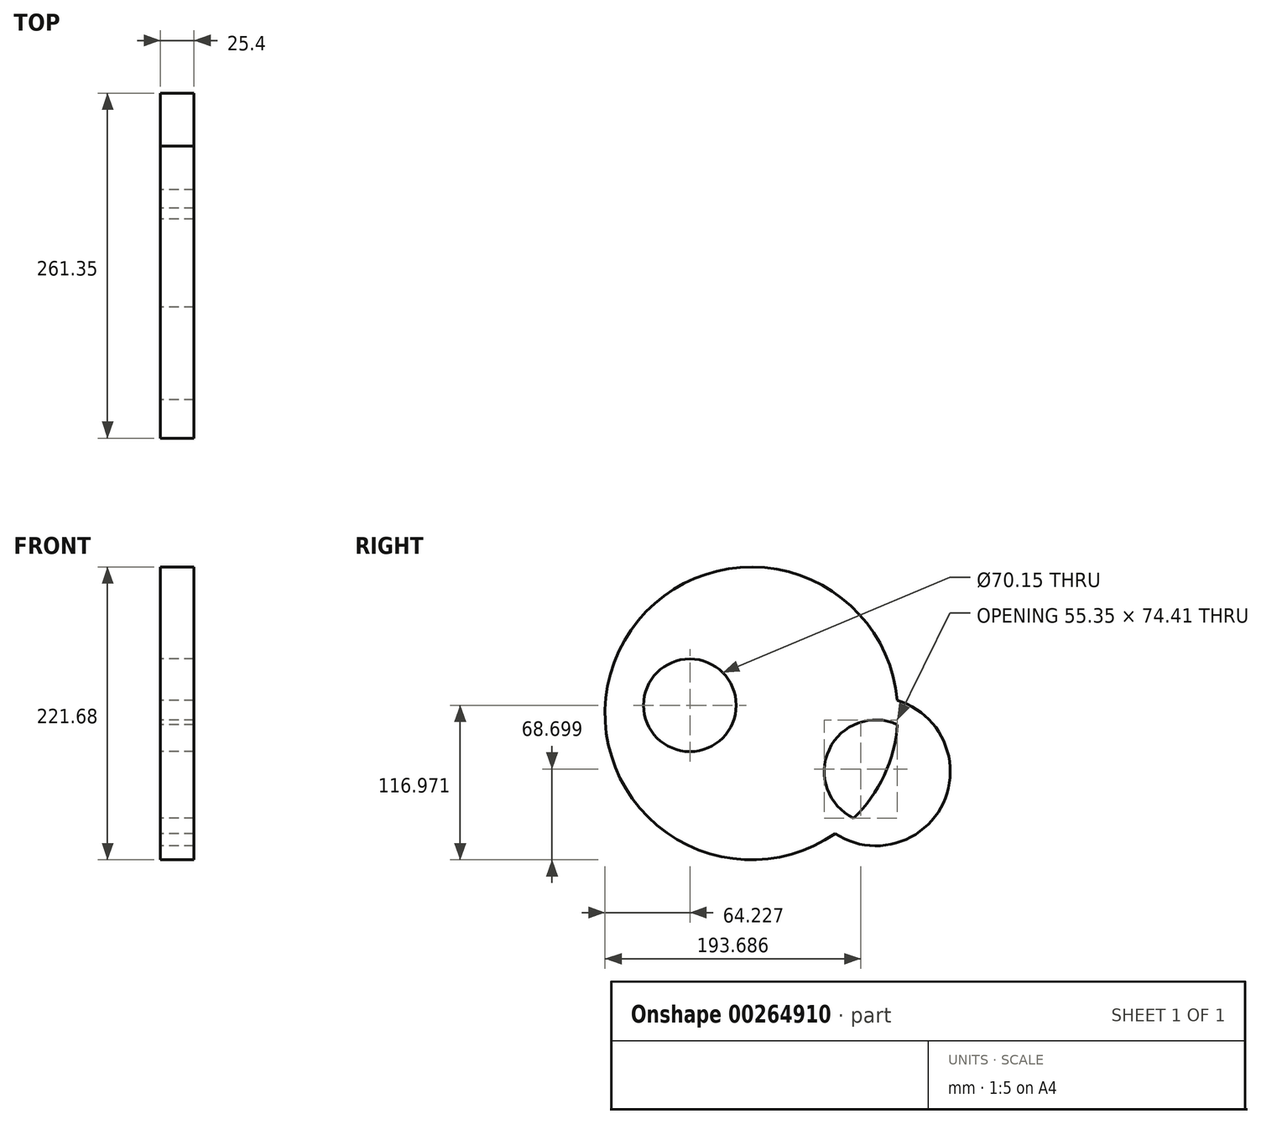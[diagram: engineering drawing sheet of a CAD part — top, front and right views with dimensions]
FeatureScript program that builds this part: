
annotation { "Feature Type Name" : "Feature", "Feature Type Description" : "" }
export const myFeature = defineFeature(function(context is Context, id is Id, definition is map)
    precondition{}
    {
        {
            var Q0;
            Q0=qCreatedBy(makeId("Right.planeOp"),FACE);
            var sketch = newSketch(context, id + "F0", { "sketchPlane" : qUnion([Q0])});
            skCircle(sketch, "E0", {"center": v(-58.46, 65.68) * mm, "radius": 56.25 * mm});
            skCircle(sketch, "E1", {"center": v(-58.46, 65.68) * mm, "radius": 39.13 * mm});
            skCircle(sketch, "E2", {"center": v(-199.33, 115.85) * mm, "radius": 35.08 * mm});
            skCircle(sketch, "E3", {"center": v(-152.72, 109.72) * mm, "radius": 110.84 * mm});
            skSolve(sketch);
        }
        {
            var Q0;
            Q0=makeQuery(id+"F0.imprint","IMPRINT",FACE,{"disambiguationData":[TD([[makeQuery(id+"F0.imprint","IMPRINT",EDGE,{"derivedFrom":sQuery(id+"F0.wireOp",EDGE,"E2")}),-1.0]])]});
            var Q1;
            {var subQ0=sQuery(id+"F0.wireOp",EDGE,"E3");var subQ1=sQuery(id+"F0.wireOp",EDGE,"E0");var subQ2=makeQuery(id+"F0.imprint","INTERSECT",VERTEX,{"disambiguationData":[OD(0.0)],"derivedFrom":[subQ1,subQ0]});Q1=makeQuery(id+"F0.imprint","IMPRINT",FACE,{"disambiguationData":[TD([[makeQuery(id+"F0.imprint","IMPRINT",EDGE,{"disambiguationData":[TD([[subQ2,-1.0]])],"derivedFrom":subQ1}),1.0]])]});}
            var Q2;
            {var subQ0=sQuery(id+"F0.wireOp",EDGE,"E3");var subQ1=sQuery(id+"F0.wireOp",EDGE,"E0");var subQ2=makeQuery(id+"F0.imprint","INTERSECT",VERTEX,{"disambiguationData":[OD(0.0)],"derivedFrom":[subQ1,subQ0]});Q2=makeQuery(id+"F0.imprint","IMPRINT",FACE,{"disambiguationData":[TD([[makeQuery(id+"F0.imprint","IMPRINT",EDGE,{"disambiguationData":[TD([[subQ2,1.0]])],"derivedFrom":subQ1}),1.0]])]});}
            var Q3;
            {var subQ0=sQuery(id+"F0.wireOp",EDGE,"E3");var subQ1=sQuery(id+"F0.wireOp",EDGE,"E1");var subQ2=makeQuery(id+"F0.imprint","INTERSECT",VERTEX,{"disambiguationData":[OD(0.0)],"derivedFrom":[subQ1,subQ0]});Q3=makeQuery(id+"F0.imprint","IMPRINT",FACE,{"disambiguationData":[TD([[makeQuery(id+"F0.imprint","IMPRINT",EDGE,{"disambiguationData":[TD([[subQ2,-1.0]])],"derivedFrom":subQ1}),1.0]])]});}
            extrude(context, id + "F1", {"entities" : qUnion([Q0, Q1, Q2, Q3]), "depth" : 25.4 * mm});
        }
    });
